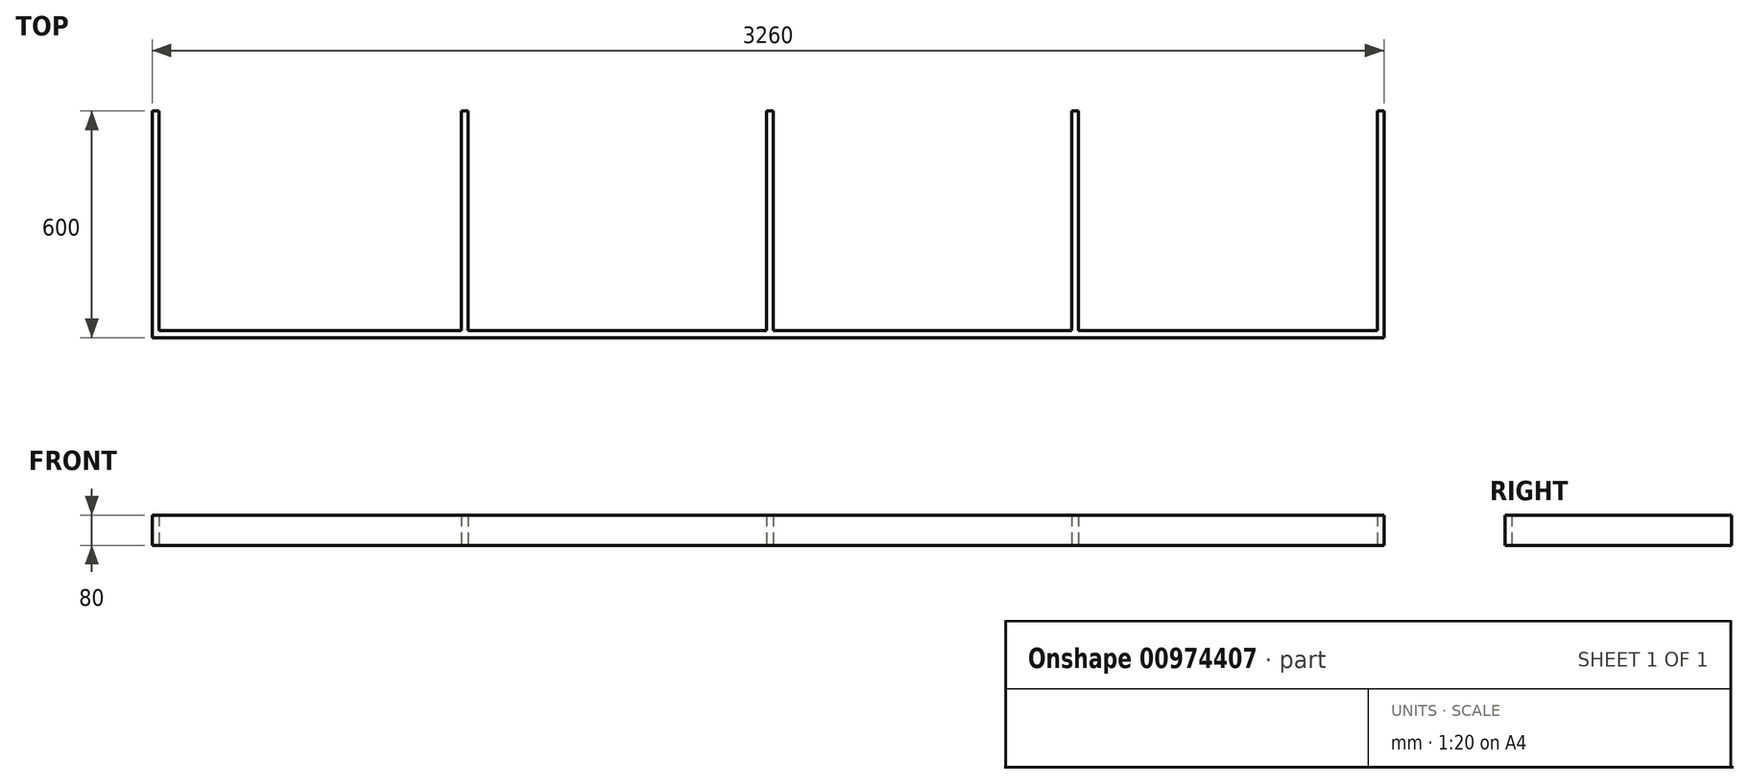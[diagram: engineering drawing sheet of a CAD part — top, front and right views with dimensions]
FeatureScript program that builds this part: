
annotation { "Feature Type Name" : "Feature", "Feature Type Description" : "" }
export const myFeature = defineFeature(function(context is Context, id is Id, definition is map)
    precondition{}
    {
        {
            var Q0;
            Q0=qCreatedBy(makeId("Top.planeOp"),FACE);
            var sketch = newSketch(context, id + "F0", { "sketchPlane" : qUnion([Q0])});
            skLineSegment(sketch, "E0", {"start": v(-1626.9, -675.67) * mm, "end": v(1633.1, -675.67) * mm});
            skLineSegment(sketch, "E1", {"start": v(1633.1, -675.67) * mm, "end": v(1633.1, -75.67) * mm});
            skLineSegment(sketch, "E2", {"start": v(1633.1, -75.67) * mm, "end": v(1615.1, -75.67) * mm});
            skLineSegment(sketch, "E3", {"start": v(1615.1, -75.67) * mm, "end": v(1615.1, -657.67) * mm});
            skLineSegment(sketch, "E4", {"start": v(1615.1, -657.67) * mm, "end": v(825.1, -657.67) * mm});
            skLineSegment(sketch, "E5", {"start": v(825.1, -657.67) * mm, "end": v(825.1, -75.67) * mm});
            skLineSegment(sketch, "E6", {"start": v(825.1, -75.67) * mm, "end": v(807.1, -75.67) * mm});
            skLineSegment(sketch, "E7", {"start": v(807.1, -75.67) * mm, "end": v(807.1, -657.67) * mm});
            skLineSegment(sketch, "E8", {"start": v(807.1, -657.67) * mm, "end": v(17.1, -657.67) * mm});
            skLineSegment(sketch, "E9", {"start": v(17.1, -657.67) * mm, "end": v(17.1, -75.67) * mm});
            skLineSegment(sketch, "E10", {"start": v(17.1, -75.67) * mm, "end": v(-0.9, -75.67) * mm});
            skLineSegment(sketch, "E11", {"start": v(-0.9, -75.67) * mm, "end": v(-0.9, -657.67) * mm});
            skLineSegment(sketch, "E12", {"start": v(-0.9, -657.67) * mm, "end": v(-790.9, -657.67) * mm});
            skLineSegment(sketch, "E13", {"start": v(-790.9, -657.67) * mm, "end": v(-790.9, -75.67) * mm});
            skLineSegment(sketch, "E14", {"start": v(-790.9, -75.67) * mm, "end": v(-808.9, -75.67) * mm});
            skLineSegment(sketch, "E15", {"start": v(-808.9, -75.67) * mm, "end": v(-808.9, -657.67) * mm});
            skLineSegment(sketch, "E16", {"start": v(-808.9, -657.67) * mm, "end": v(-1608.9, -657.67) * mm});
            skLineSegment(sketch, "E17", {"start": v(-1608.9, -657.67) * mm, "end": v(-1608.9, -75.67) * mm});
            skLineSegment(sketch, "E18", {"start": v(-1608.9, -75.67) * mm, "end": v(-1626.9, -75.67) * mm});
            skLineSegment(sketch, "E19", {"start": v(-1626.9, -75.67) * mm, "end": v(-1626.9, -675.67) * mm});
            skSolve(sketch);
        }
        {
            var Q0;
            Q0=makeQuery(id+"F0.imprint","IMPRINT",FACE,{"disambiguationData":[TD([[makeQuery(id+"F0.imprint","IMPRINT",EDGE,{"derivedFrom":sQuery(id+"F0.wireOp",EDGE,"E0")}),1.0]])]});
            extrude(context, id + "F1", {"entities" : qUnion([Q0]), "depth" : 80 * mm, "offsetDistance" : 25 * mm});
        }
    });
